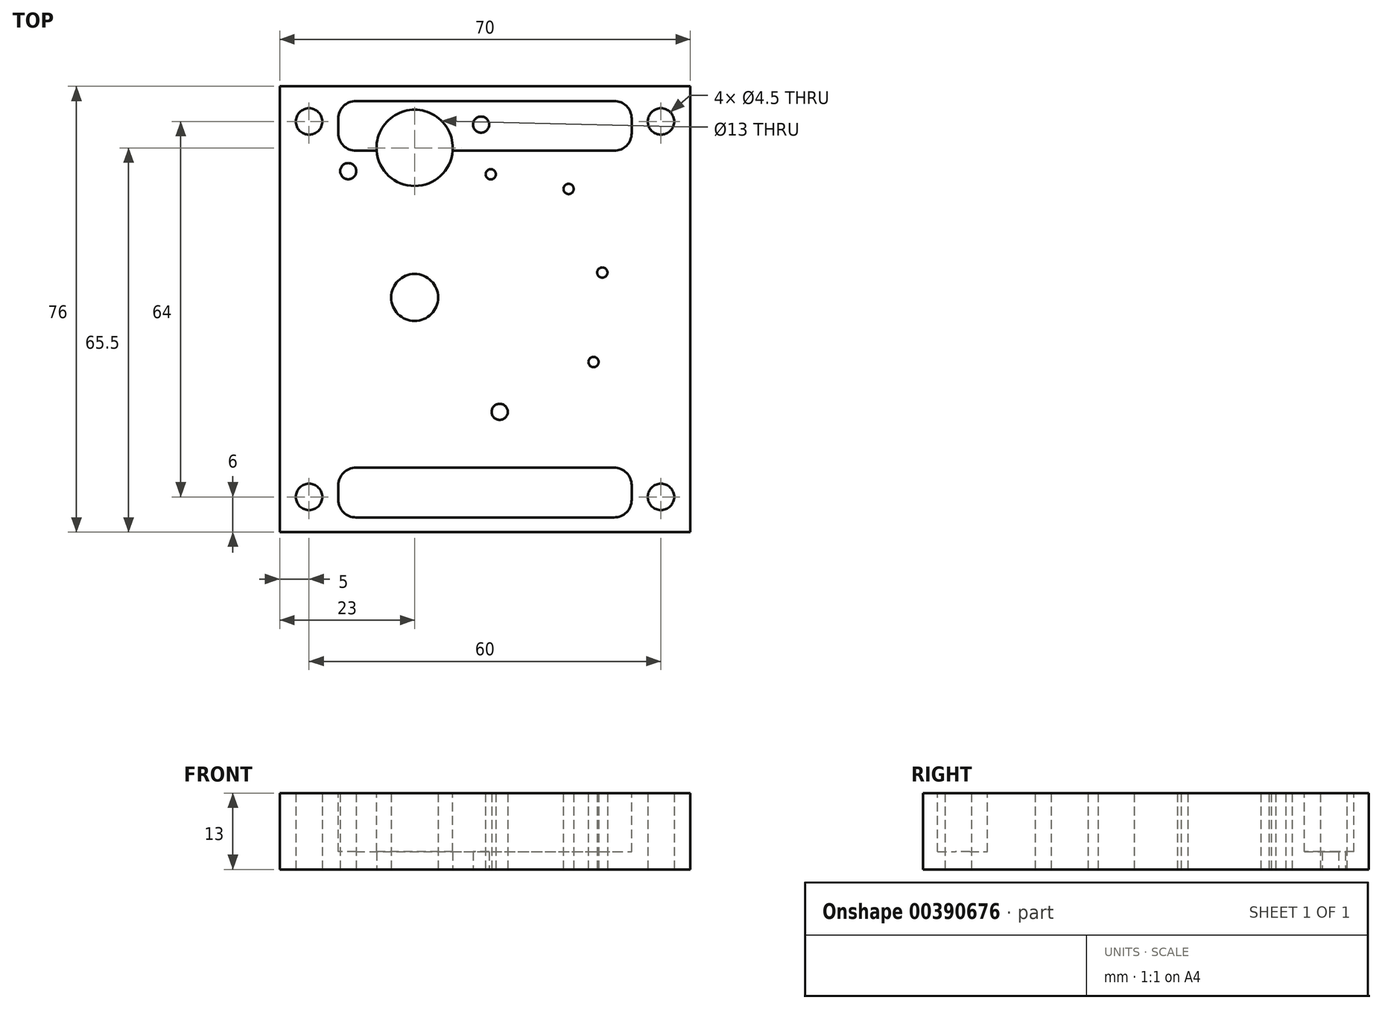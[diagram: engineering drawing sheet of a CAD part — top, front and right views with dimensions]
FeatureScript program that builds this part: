
annotation { "Feature Type Name" : "Feature", "Feature Type Description" : "" }
export const myFeature = defineFeature(function(context is Context, id is Id, definition is map)
    precondition{}
    {
        {
            var Q0;
            Q0=qCreatedBy(makeId("Top.planeOp"),FACE);
            var sketch = newSketch(context, id + "F0", { "sketchPlane" : qUnion([Q0])});
            skLineSegment(sketch, "E0.bottom", {"start": v(-35, 38) * mm, "end": v(35, 38) * mm});
            skLineSegment(sketch, "E0.top", {"start": v(-35, -38) * mm, "end": v(35, -38) * mm});
            skLineSegment(sketch, "E0.left", {"start": v(-35, 38) * mm, "end": v(-35, -38) * mm});
            skLineSegment(sketch, "E0.right", {"start": v(35, 38) * mm, "end": v(35, -38) * mm});
            skCircle(sketch, "E1", {"center": v(-30, 32) * mm, "radius": 2.25 * mm});
            skCircle(sketch, "E2.MirrorC", {"center": v(30, 32) * mm, "radius": 2.25 * mm});
            skCircle(sketch, "E3.MirrorC", {"center": v(-30, -32) * mm, "radius": 2.25 * mm});
            skCircle(sketch, "E4.MirrorC", {"center": v(30, -32) * mm, "radius": 2.25 * mm});
            skCircle(sketch, "E5", {"center": v(-12, 2) * mm, "radius": 4 * mm});
            skCircle(sketch, "E6", {"center": v(2.5, -17.5) * mm, "radius": 1.38 * mm});
            skCircle(sketch, "E7", {"center": v(18.5, -9) * mm, "radius": 0.88 * mm});
            skCircle(sketch, "E8", {"center": v(20, 6.25) * mm, "radius": 0.87 * mm});
            skCircle(sketch, "E9", {"center": v(14.25, 20.5) * mm, "radius": 0.87 * mm});
            skCircle(sketch, "E10", {"center": v(-12, 2) * mm, "radius": 21 * mm, "construction": true});
            skCircle(sketch, "E11", {"center": v(14.25, 20.5) * mm, "radius": 5.5 * mm, "construction": true});
            skCircle(sketch, "E12", {"center": v(20, 6.25) * mm, "radius": 11 * mm, "construction": true});
            skCircle(sketch, "E13", {"center": v(14.25, 20.5) * mm, "radius": 10.75 * mm, "construction": true});
            skCircle(sketch, "E14", {"center": v(0.98, 23) * mm, "radius": 2.75 * mm, "construction": true});
            skCircle(sketch, "E15", {"center": v(0.98, 23) * mm, "radius": 0.88 * mm});
            skCircle(sketch, "E16", {"center": v(0.98, 23) * mm, "radius": 10.75 * mm, "construction": true});
            skCircle(sketch, "E17", {"center": v(-12, 27.5) * mm, "radius": 3 * mm, "construction": true});
            skCircle(sketch, "E18", {"center": v(-12, 27.5) * mm, "radius": 6.5 * mm});
            skCircle(sketch, "E19", {"center": v(-0.67, 31.47) * mm, "radius": 1.38 * mm});
            skLineSegment(sketch, "E20", {"start": v(-0.67, 31.47) * mm, "end": v(-12, 27.5) * mm, "construction": true});
            skLineSegment(sketch, "E21", {"start": v(-12, 27.5) * mm, "end": v(-23.33, 23.53) * mm, "construction": true});
            skCircle(sketch, "E22", {"center": v(-23.33, 23.53) * mm, "radius": 1.38 * mm});
            skSolve(sketch);
        }
        {
            var Q0;
            Q0=qSketchRegion(id+"F0",true);
            extrude(context, id + "F1", {"entities" : qUnion([Q0]), "depth" : 13 * mm, "offsetDistance" : 25 * mm});
        }
        {
            var Q0;
            Q0=makeQuery(id+"F1.opExtrude","CAP_FACE",FACE,{"disambiguationData":[OSD([sQuery(id+"F0.wireOp",EDGE,"E0.bottom"),sQuery(id+"F0.wireOp",EDGE,"E0.top"),sQuery(id+"F0.wireOp",EDGE,"E0.left"),sQuery(id+"F0.wireOp",EDGE,"E0.right"),sQuery(id+"F0.wireOp",EDGE,"E1"),sQuery(id+"F0.wireOp",EDGE,"E2.MirrorC"),sQuery(id+"F0.wireOp",EDGE,"E3.MirrorC"),sQuery(id+"F0.wireOp",EDGE,"E4.MirrorC")])],"isStart":false});
            var sketch = newSketch(context, id + "F2", { "sketchPlane" : qUnion([Q0])});
            skLineSegment(sketch, "E23.bottom", {"start": v(-32.5, 27) * mm, "end": v(32.5, 27) * mm});
            skLineSegment(sketch, "E23.top", {"start": v(-32.5, -27) * mm, "end": v(32.5, -27) * mm});
            skLineSegment(sketch, "E23.left", {"start": v(-32.5, 27) * mm, "end": v(-32.5, -27) * mm});
            skLineSegment(sketch, "E23.right", {"start": v(32.5, 27) * mm, "end": v(32.5, -27) * mm});
            skLineSegment(sketch, "E24.bottom", {"start": v(-25, 27) * mm, "end": v(25, 27) * mm});
            skLineSegment(sketch, "E24.top", {"start": v(-25, 35.5) * mm, "end": v(25, 35.5) * mm});
            skLineSegment(sketch, "E24.left", {"start": v(-25, 27) * mm, "end": v(-25, 35.5) * mm});
            skLineSegment(sketch, "E24.right", {"start": v(25, 27) * mm, "end": v(25, 35.5) * mm});
            skLineSegment(sketch, "E25.MirrorCS", {"start": v(-25, -27) * mm, "end": v(-25, -35.5) * mm});
            skLineSegment(sketch, "E26.MirrorCS", {"start": v(-25, -35.5) * mm, "end": v(25, -35.5) * mm});
            skLineSegment(sketch, "E27.MirrorCS", {"start": v(25, -27) * mm, "end": v(25, -35.5) * mm});
            skSolve(sketch);
        }
        {
            var Q0;
            {var subQ1=sQuery(id+"F2.wireOp",EDGE,"E23.left");Q0=makeQuery(id+"F2.imprint","IMPRINT",FACE,{"disambiguationData":[TD([[makeQuery(id+"F2.imprint","IMPRINT",EDGE,{"derivedFrom":subQ1}),1.0]])]});}
            var Q1;
            Q1=makeQuery(id+"F2.imprint","IMPRINT",FACE,{"disambiguationData":[TD([[makeQuery(id+"F2.imprint","IMPRINT",EDGE,{"derivedFrom":sQuery(id+"F2.wireOp",EDGE,"E24.top")}),-1.0]])]});
            var Q2;
            {var subQ0=sQuery(id+"F2.wireOp",EDGE,"E25.MirrorCS");Q2=makeQuery(id+"F2.imprint","IMPRINT",FACE,{"disambiguationData":[TD([[makeQuery(id+"F2.imprint","IMPRINT",EDGE,{"derivedFrom":subQ0}),1.0]])]});}
            extrude(context, id + "F3", {"entities" : qUnion([Q0, Q1, Q2]), "operationType" : NewBodyOperationType.REMOVE, "oppositeDirection" : true, "depth" : 10 * mm, "offsetDistance" : 25 * mm});
        }
        {
            var Q0;
            Q0=makeQuery(id+"F3.boolean.opBoolean","COPY",EDGE,{"derivedFrom":makeQuery(id+"F3.opExtrude","SWEPT_EDGE",EDGE,{"disambiguationData":[OSD([sQuery(id+"F2.wireOp",EDGE,"E23.bottom"),sQuery(id+"F2.wireOp",EDGE,"E24.left")])]})});
            var Q1;
            Q1=makeQuery(id+"F3.boolean.opBoolean","COPY",EDGE,{"derivedFrom":makeQuery(id+"F3.opExtrude","SWEPT_EDGE",EDGE,{"disambiguationData":[OSD([sQuery(id+"F2.wireOp",EDGE,"E23.bottom"),sQuery(id+"F2.wireOp",EDGE,"E24.right")])]})});
            var Q2;
            Q2=makeQuery(id+"F3.boolean.opBoolean","COPY",EDGE,{"derivedFrom":makeQuery(id+"F3.opExtrude","SWEPT_EDGE",EDGE,{"disambiguationData":[OSD([sQuery(id+"F2.wireOp",EDGE,"E23.top"),sQuery(id+"F2.wireOp",EDGE,"E25.MirrorCS")])]})});
            var Q3;
            Q3=makeQuery(id+"F3.boolean.opBoolean","COPY",EDGE,{"derivedFrom":makeQuery(id+"F3.opExtrude","SWEPT_EDGE",EDGE,{"disambiguationData":[OSD([sQuery(id+"F2.wireOp",EDGE,"E23.top"),sQuery(id+"F2.wireOp",EDGE,"E27.MirrorCS")])]})});
            var Q4;
            Q4=makeQuery(id+"F3.boolean.opBoolean","COPY",EDGE,{"derivedFrom":makeQuery(id+"F3.opExtrude","SWEPT_EDGE",EDGE,{"disambiguationData":[OSD([sQuery(id+"F2.wireOp",EDGE,"E23.top"),sQuery(id+"F2.wireOp",EDGE,"E23.right")])]})});
            var Q5;
            Q5=makeQuery(id+"F3.boolean.opBoolean","COPY",EDGE,{"derivedFrom":makeQuery(id+"F3.opExtrude","SWEPT_EDGE",EDGE,{"disambiguationData":[OSD([sQuery(id+"F2.wireOp",EDGE,"E23.bottom"),sQuery(id+"F2.wireOp",EDGE,"E23.right")])]})});
            var Q6;
            Q6=makeQuery(id+"F3.boolean.opBoolean","COPY",EDGE,{"derivedFrom":makeQuery(id+"F3.opExtrude","SWEPT_EDGE",EDGE,{"disambiguationData":[OSD([sQuery(id+"F2.wireOp",EDGE,"E24.top"),sQuery(id+"F2.wireOp",EDGE,"E24.right")])]})});
            var Q7;
            Q7=makeQuery(id+"F3.boolean.opBoolean","COPY",EDGE,{"derivedFrom":makeQuery(id+"F3.opExtrude","SWEPT_EDGE",EDGE,{"disambiguationData":[OSD([sQuery(id+"F2.wireOp",EDGE,"E24.top"),sQuery(id+"F2.wireOp",EDGE,"E24.left")])]})});
            var Q8;
            Q8=makeQuery(id+"F3.boolean.opBoolean","COPY",EDGE,{"derivedFrom":makeQuery(id+"F3.opExtrude","SWEPT_EDGE",EDGE,{"disambiguationData":[OSD([sQuery(id+"F2.wireOp",EDGE,"E23.bottom"),sQuery(id+"F2.wireOp",EDGE,"E23.left")])]})});
            var Q9;
            Q9=makeQuery(id+"F3.boolean.opBoolean","COPY",EDGE,{"derivedFrom":makeQuery(id+"F3.opExtrude","SWEPT_EDGE",EDGE,{"disambiguationData":[OSD([sQuery(id+"F2.wireOp",EDGE,"E23.top"),sQuery(id+"F2.wireOp",EDGE,"E23.left")])]})});
            var Q10;
            Q10=makeQuery(id+"F3.boolean.opBoolean","COPY",EDGE,{"derivedFrom":makeQuery(id+"F3.opExtrude","SWEPT_EDGE",EDGE,{"disambiguationData":[OSD([sQuery(id+"F2.wireOp",EDGE,"E25.MirrorCS"),sQuery(id+"F2.wireOp",EDGE,"E26.MirrorCS")])]})});
            var Q11;
            Q11=makeQuery(id+"F3.boolean.opBoolean","COPY",EDGE,{"derivedFrom":makeQuery(id+"F3.opExtrude","SWEPT_EDGE",EDGE,{"disambiguationData":[OSD([sQuery(id+"F2.wireOp",EDGE,"E26.MirrorCS"),sQuery(id+"F2.wireOp",EDGE,"E27.MirrorCS")])]})});
            fillet(context, id + "F4", {"entities" : qUnion([Q0, Q1, Q2, Q3, Q4, Q5, Q6, Q7, Q8, Q9, Q10, Q11]), "radius" : 3 * mm, "tangentPropagation" : true, "allowEdgeOverflow" : false});
        }
    });
